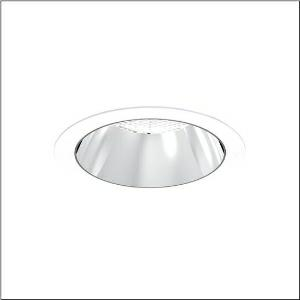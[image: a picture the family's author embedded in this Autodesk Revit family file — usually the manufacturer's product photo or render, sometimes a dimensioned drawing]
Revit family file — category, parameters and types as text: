
# Revit family: lunis_21_xl_51db15mf91c
name_source: partatom
category: Lighting Fixtures
units: mm (PartAtom-declared; Revit-internal decimal feet)

## family parameters
Cut with Voids When Loaded = No
Host = Face
Light Source = No
Part Type = Normal
Room Calculation Point = No
Round Connector Dimension = Use Diameter
Shared = No

## types (1)
- --- (1 x LED, 3740 lm, 21.7 W, 6500K)
    Apparent Load = 22 VA
    CIE Flux Codes = 92 100 100 100 100
    Color Rendering = 80
    Color Temperature = 6500K
    Default Elevation = 1800 mm
    Description = Lunis 21,  XL, downlight, light control with lens, of PMMA, anti glare with reflector, of PC, highly specular, light emission: direct distribution, LED rated luminous flux: 2.510lm, light colour: 830/840/865, with terminal, 3-pole, mains connection: 220..240V, AC/DC, 0/50..60Hz, housing, round, of diecast aluminium, traffic white (RAL 9016), diameter: 230mm, clamping range: 1..40mm, protection rating (complete): IP20, protection rating (on room side): IP54, insulation class (complete): insulation class II (safety insulation), certification: CE, impact resistance: IK03, packaging unit: 1 piece
    Height = 0 mm  [stored 0 ft]
    Lamp = 1 x LED
    Lamp Light Flux = 3740 lm
    Lamp Power = 21.7 W
    Lamp count = 1
    Length = 230 mm
    Luminous efficacy = 172 lm/W
    Manufacturer = Siteco
    ModVariant = No
    Model = 51DB15MF91C
    Mounting Place = Ceiling
    Mounting Type = Recessed
    Number of Poles = 1
    OnlyDefault = Yes
    Power Factor = 1
    Product Name = Lunis 21 XL
    Product group = downlight
    ProductGroupID = 400
    Protection Class = Protection class II
    Protection Degree = IP 20
    RLX_Detail_Level = 1
    RLX_Emergency_Light_Flux = 0 lm
    RLX_Emergency_Type = 0
    RLX_Emergency_Type_DB = No
    RlxData = <blob elided: 20069 chars, md5=62551186>
    Socket = socket
    Standby Power = 0 W
    System Light Flux = 3740 lm
    System Power = 22 W
    Type Comments = individual setting: colour temperature 6500K, luminous flux: 100 % | (OFF | ON | ON | ON) | 650 mA
    Type Image = l_1291156.jpg
    URL = http://relux.com
    VarID = @adj_020344
    Voltage = 0 V
    Weight = 0.00 kg
    Width = 0 mm  [stored 0 ft]

note: [stored X ft] marks values corroborated as IEEE doubles in the binary element streams (Revit-internal decimal feet)

## geometry (parser evidence)
native form markers: Blend x4, Sweep x11
no freeform markers — native parametric forms only
